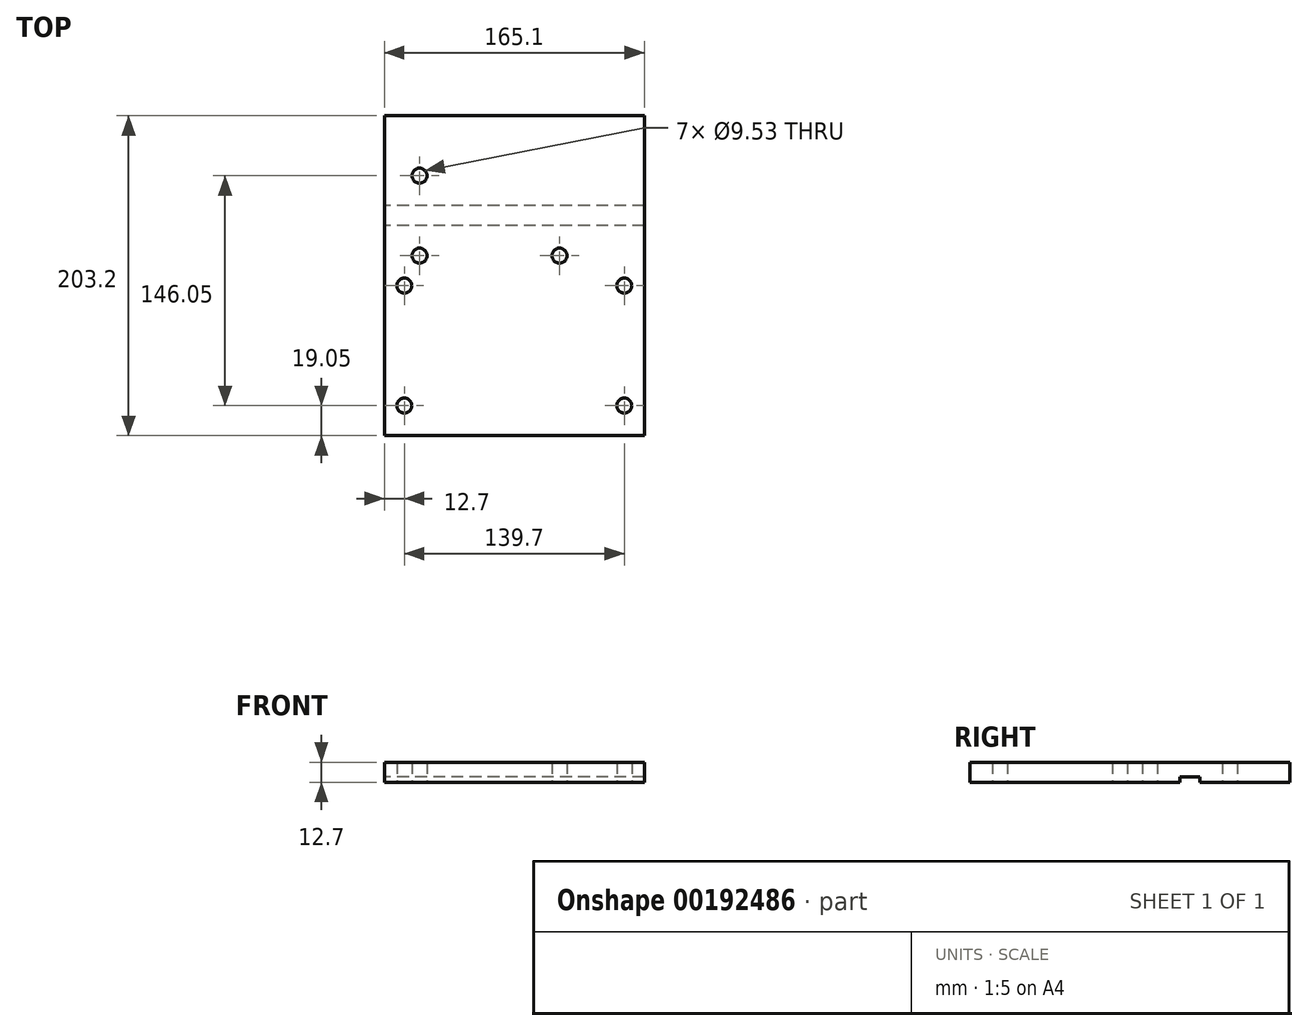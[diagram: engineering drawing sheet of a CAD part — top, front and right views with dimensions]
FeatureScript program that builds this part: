
annotation { "Feature Type Name" : "Feature", "Feature Type Description" : "" }
export const myFeature = defineFeature(function(context is Context, id is Id, definition is map)
    precondition{}
    {
        {
            var Q0;
            Q0=qCreatedBy(makeId("Top.planeOp"),FACE);
            var sketch = newSketch(context, id + "F0", { "sketchPlane" : qUnion([Q0])});
            skLineSegment(sketch, "E0.bottom", {"start": v(82.55, 101.6) * mm, "end": v(-82.55, 101.6) * mm});
            skLineSegment(sketch, "E0.top", {"start": v(82.55, -101.6) * mm, "end": v(-82.55, -101.6) * mm});
            skLineSegment(sketch, "E0.left", {"start": v(82.55, 101.6) * mm, "end": v(82.55, -101.6) * mm});
            skLineSegment(sketch, "E0.right", {"start": v(-82.55, 101.6) * mm, "end": v(-82.55, -101.6) * mm});
            skPoint(sketch, "E0.middle", {"position": v(0, 0) * mm});
            skCircle(sketch, "E1", {"center": v(69.85, -82.55) * mm, "radius": 4.76 * mm});
            skCircle(sketch, "E2", {"center": v(69.85, -6.35) * mm, "radius": 4.76 * mm});
            skCircle(sketch, "E3.MirrorC", {"center": v(-60.2, 63.5) * mm, "radius": 4.76 * mm});
            skCircle(sketch, "E4.MirrorC", {"center": v(-60.2, 12.7) * mm, "radius": 4.76 * mm});
            skCircle(sketch, "E5.MirrorC", {"center": v(28.7, 12.7) * mm, "radius": 4.76 * mm});
            skCircle(sketch, "E6.MirrorC", {"center": v(-69.85, -6.35) * mm, "radius": 4.76 * mm});
            skCircle(sketch, "E7.MirrorC", {"center": v(-69.85, -82.55) * mm, "radius": 4.76 * mm});
            skSolve(sketch);
        }
        {
            var Q0;
            Q0 = qSketchRegion(id + "F0", true);
            extrude(context, id + "F1", {"entities" : qUnion([Q0]), "depth" : 12.7 * mm});
        }
        {
            var Q0;
            Q0=makeQuery(id+"F1.opExtrude","SWEPT_FACE",FACE,{"disambiguationData":[OSD([sQuery(id+"F0.wireOp",EDGE,"E0.right")])]});
            var sketch = newSketch(context, id + "F2", { "sketchPlane" : qUnion([Q0])});
            skLineSegment(sketch, "E8", {"start": v(-44.45, 0) * mm, "end": v(-44.45, 3.3) * mm});
            skLineSegment(sketch, "E9", {"start": v(-44.45, 3.3) * mm, "end": v(-31.75, 3.3) * mm});
            skLineSegment(sketch, "E10", {"start": v(-31.75, 3.3) * mm, "end": v(-31.75, 0) * mm});
            skLineSegment(sketch, "E11", {"start": v(-31.75, 0) * mm, "end": v(-44.45, 0) * mm});
            skSolve(sketch);
        }
        {
            var Q0;
            Q0 = qSketchRegion(id + "F2", true);
            extrude(context, id + "F3", {"entities" : qUnion([Q0]), "operationType" : NewBodyOperationType.REMOVE, "endBound" : BoundingType.THROUGH_ALL, "oppositeDirection" : true, "depth" : 25.4 * mm});
        }
    });
